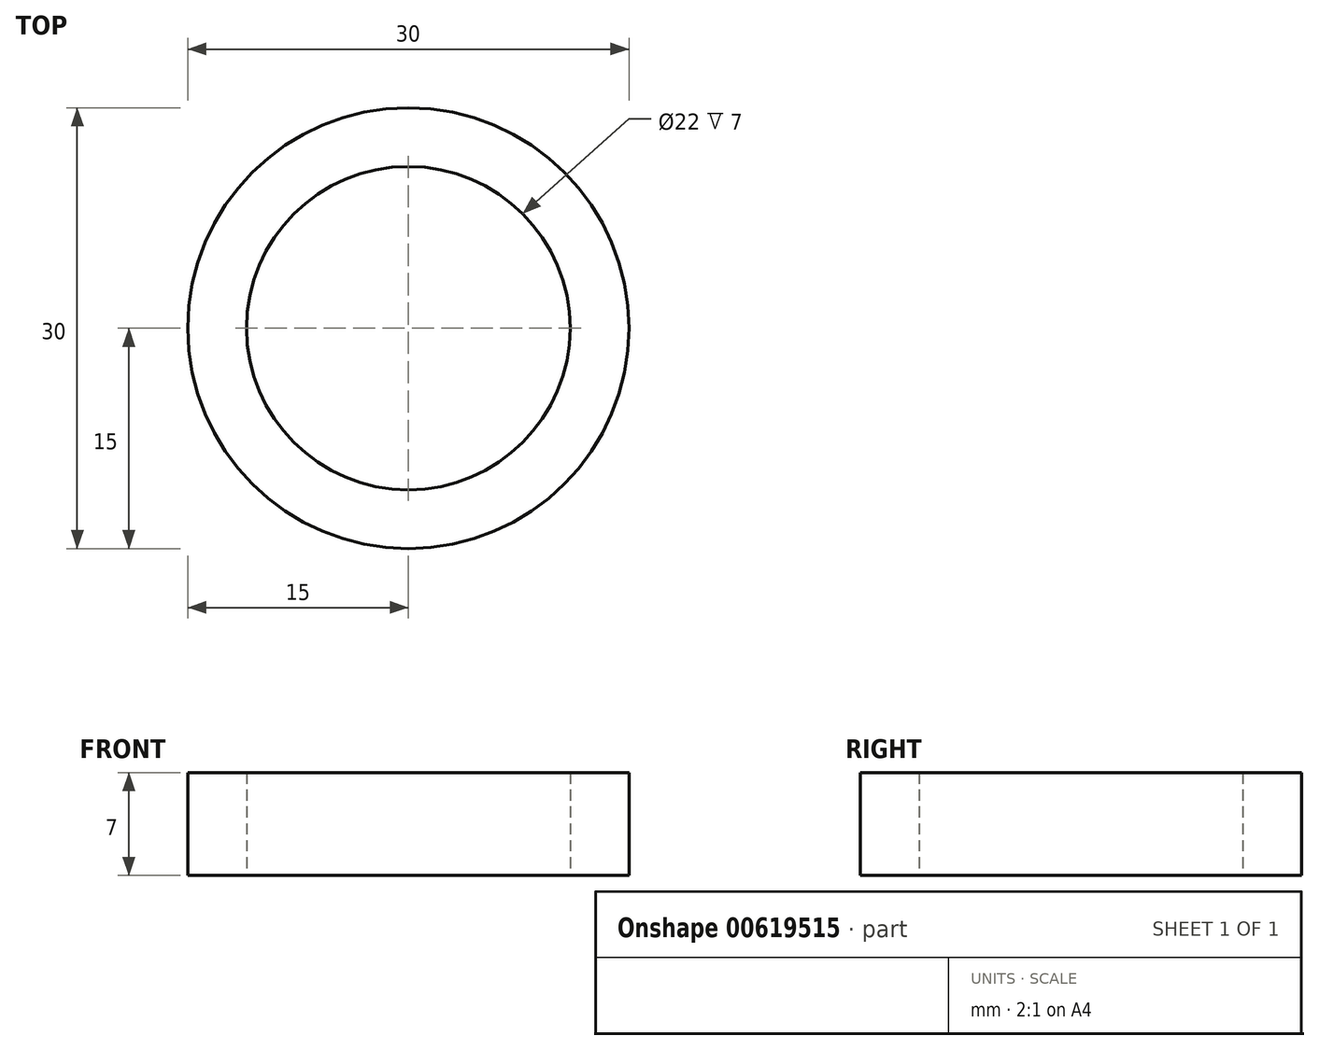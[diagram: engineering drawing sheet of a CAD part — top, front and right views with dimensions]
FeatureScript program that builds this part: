
annotation { "Feature Type Name" : "Feature", "Feature Type Description" : "" }
export const myFeature = defineFeature(function(context is Context, id is Id, definition is map)
    precondition{}
    {
        {
            var Q0;
            Q0=qCreatedBy(makeId("Top.planeOp"),FACE);
            var sketch = newSketch(context, id + "F0", { "sketchPlane" : qUnion([Q0])});
            skCircle(sketch, "E0", {"center": v(0, 0) * mm, "radius": 11 * mm});
            skCircle(sketch, "E1", {"center": v(0, 0) * mm, "radius": 15 * mm});
            skSolve(sketch);
        }
        {
            var Q0;
            Q0 = qSketchRegion(id + "F0", true);
            extrude(context, id + "F1", {"entities" : qUnion([Q0]), "depth" : 7 * mm, "offsetDistance" : 25 * mm});
        }
    });
